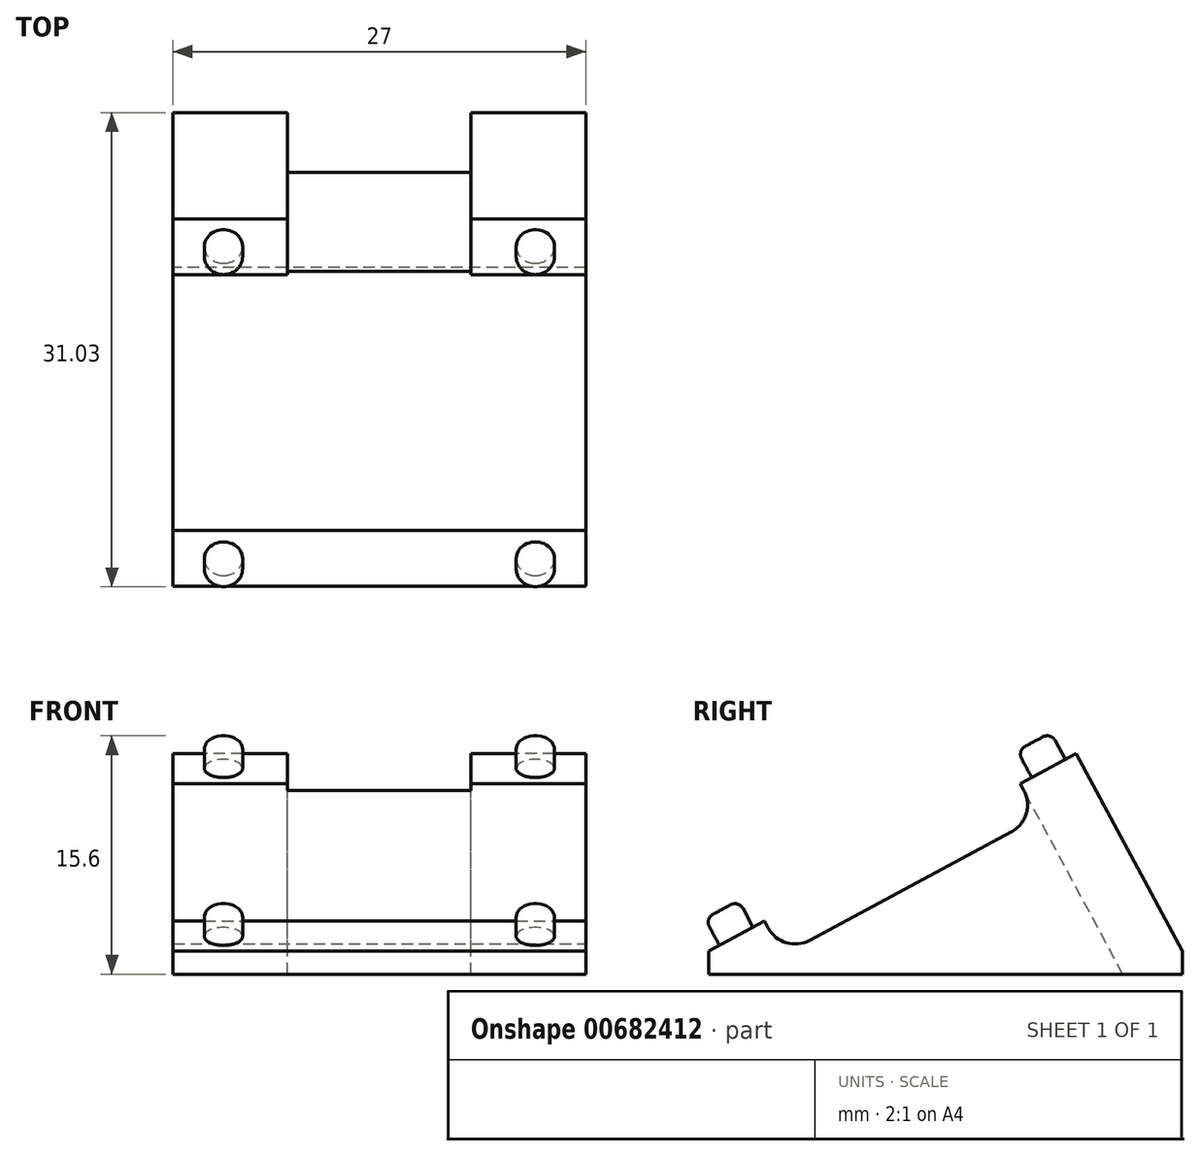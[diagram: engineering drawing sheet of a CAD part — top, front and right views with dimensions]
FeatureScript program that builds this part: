
annotation { "Feature Type Name" : "Feature", "Feature Type Description" : "" }
export const myFeature = defineFeature(function(context is Context, id is Id, definition is map)
    precondition{}
    {
        {
            var Q0;
            Q0=qCreatedBy(makeId("Top.planeOp"),FACE);
            var sketch = newSketch(context, id + "F0", { "sketchPlane" : qUnion([Q0])});
            skLineSegment(sketch, "E0.bottom", {"start": v(-16.53, 19.77) * mm, "end": v(10.47, 19.77) * mm});
            skLineSegment(sketch, "E0.top", {"start": v(-16.53, -11.23) * mm, "end": v(10.47, -11.23) * mm});
            skLineSegment(sketch, "E0.left", {"start": v(-16.53, 19.77) * mm, "end": v(-16.53, -11.23) * mm});
            skLineSegment(sketch, "E0.right", {"start": v(10.47, 19.77) * mm, "end": v(10.47, -11.23) * mm});
            skSolve(sketch);
        }
        {
            var Q0;
            Q0=makeQuery(id+"F0.imprint","IMPRINT",FACE,{"disambiguationData":[TD([[makeQuery(id+"F0.imprint","IMPRINT",EDGE,{"derivedFrom":sQuery(id+"F0.wireOp",EDGE,"E0.bottom")}),-1.0]])]});
            extrude(context, id + "F1", {"entities" : qUnion([Q0]), "depth" : 1.5 * mm, "offsetDistance" : 25 * mm});
        }
        {
            var Q0;
            Q0=makeQuery(id+"F1.opExtrude","SWEPT_FACE",FACE,{"disambiguationData":[OSD([sQuery(id+"F0.wireOp",EDGE,"E0.left")])]});
            var sketch = newSketch(context, id + "F2", { "sketchPlane" : qUnion([Q0])});
            skLineSegment(sketch, "E1", {"start": v(11.23, 1.5) * mm, "end": v(-12.82, 14.43) * mm});
            skLineSegment(sketch, "E2", {"start": v(-12.82, 14.43) * mm, "end": v(-19.77, 1.5) * mm});
            skSolve(sketch);
        }
        {
            var Q0;
            Q0=makeQuery(id+"F2.imprint","IMPRINT",FACE,{"disambiguationData":[TD([[makeQuery(id+"F2.imprint","IMPRINT",EDGE,{"derivedFrom":sQuery(id+"F2.wireOp",EDGE,"E1")}),1.0]])]});
            extrude(context, id + "F3", {"entities" : qUnion([Q0]), "operationType" : NewBodyOperationType.ADD, "oppositeDirection" : true, "depth" : 27 * mm, "offsetDistance" : 25 * mm});
        }
        {
            var Q0;
            Q0=makeQuery(id+"F3.opExtrude","SWEPT_FACE",FACE,{"disambiguationData":[OSD([sQuery(id+"F2.wireOp",EDGE,"E1")])]});
            var sketch = newSketch(context, id + "F4", { "sketchPlane" : qUnion([Q0])});
            skLineSegment(sketch, "E3.bottom", {"start": v(-16.53, 13.98) * mm, "end": v(10.47, 13.98) * mm});
            skLineSegment(sketch, "E3.top", {"start": v(-16.53, -5.02) * mm, "end": v(10.47, -5.02) * mm});
            skLineSegment(sketch, "E3.left", {"start": v(-16.53, 13.98) * mm, "end": v(-16.53, -5.02) * mm});
            skLineSegment(sketch, "E3.right", {"start": v(10.47, 13.98) * mm, "end": v(10.47, -5.02) * mm});
            skPoint(sketch, "E4", {"position": v(-16.53, 4.48) * mm});
            skSolve(sketch);
        }
        {
            var Q0;
            Q0=makeQuery(id+"F4.imprint","IMPRINT",FACE,{"disambiguationData":[TD([[makeQuery(id+"F4.imprint","IMPRINT",EDGE,{"derivedFrom":sQuery(id+"F4.wireOp",EDGE,"E3.bottom")}),-1.0]])]});
            extrude(context, id + "F5", {"entities" : qUnion([Q0]), "operationType" : NewBodyOperationType.REMOVE, "oppositeDirection" : true, "depth" : 2.5 * mm, "offsetDistance" : 25 * mm});
        }
        {
            var Q0;
            Q0=makeQuery(id+"F5.boolean.opBoolean","COPY",EDGE,{"derivedFrom":makeQuery(id+"F5.opExtrude","CAP_EDGE",EDGE,{"disambiguationData":[OSD([sQuery(id+"F4.wireOp",EDGE,"E3.bottom")])],"isStart":false})});
            var Q1;
            Q1=makeQuery(id+"F5.boolean.opBoolean","COPY",EDGE,{"derivedFrom":makeQuery(id+"F5.opExtrude","CAP_EDGE",EDGE,{"disambiguationData":[OSD([sQuery(id+"F4.wireOp",EDGE,"E3.top")])],"isStart":false})});
            fillet(context, id + "F6", {"entities" : qUnion([Q0, Q1]), "radius" : 2 * mm, "tangentPropagation" : true, "allowEdgeOverflow" : false});
        }
        {
            var Q0;
            {var subQ0=sQuery(id+"F2.wireOp",EDGE,"E2");var subQ1=sQuery(id+"F2.wireOp",EDGE,"E1");Q0=makeQuery(id+"F5.boolean.opBoolean","SPLIT",FACE,{"disambiguationData":[TD([makeQuery(id+"F3.opExtrude","SWEPT_FACE",FACE,{"disambiguationData":[OSD([subQ0])]})])],"derivedFrom":makeQuery(id+"F3.opExtrude","SWEPT_FACE",FACE,{"disambiguationData":[OSD([subQ1])]})});}
            var sketch = newSketch(context, id + "F7", { "sketchPlane" : qUnion([Q0])});
            skLineSegment(sketch, "E5.bottom", {"start": v(-9.03, 18.13) * mm, "end": v(2.97, 18.13) * mm});
            skLineSegment(sketch, "E5.top", {"start": v(-9.03, 13.98) * mm, "end": v(2.97, 13.98) * mm});
            skLineSegment(sketch, "E5.left", {"start": v(-9.03, 18.13) * mm, "end": v(-9.03, 13.98) * mm});
            skLineSegment(sketch, "E5.right", {"start": v(2.97, 18.13) * mm, "end": v(2.97, 13.98) * mm});
            skPoint(sketch, "E6", {"position": v(-3.03, 18.13) * mm});
            skSolve(sketch);
        }
        {
            var Q0;
            Q0 = qSketchRegion(id + "F7", true);
            extrude(context, id + "F8", {"entities" : qUnion([Q0]), "operationType" : NewBodyOperationType.REMOVE, "oppositeDirection" : true, "depth" : 25 * mm, "offsetDistance" : 25 * mm});
        }
        {
            var Q0;
            {var subQ1=sQuery(id+"F2.wireOp",EDGE,"E2");var subQ2=makeQuery(id+"F3.opExtrude","SWEPT_FACE",FACE,{"disambiguationData":[OSD([subQ1])]});var subQ3=sQuery(id+"F0.wireOp",EDGE,"E0.left");var subQ4=makeQuery(id+"F1.opExtrude","SWEPT_FACE",FACE,{"disambiguationData":[OSD([subQ3])]});var subQ5=sQuery(id+"F2.wireOp",EDGE,"E1");Q0=makeQuery(id+"F8.boolean.opBoolean","SPLIT",FACE,{"disambiguationData":[TD([subQ4])],"derivedFrom":makeQuery(id+"F5.boolean.opBoolean","SPLIT",FACE,{"disambiguationData":[TD([subQ2])],"derivedFrom":makeQuery(id+"F3.opExtrude","SWEPT_FACE",FACE,{"disambiguationData":[OSD([subQ5])]})})});}
            var sketch = newSketch(context, id + "F9", { "sketchPlane" : qUnion([Q0])});
            skCircle(sketch, "E7", {"center": v(-13.23, 16.08) * mm, "radius": 1.25 * mm});
            skCircle(sketch, "E8", {"center": v(7.17, 16.08) * mm, "radius": 1.25 * mm});
            skCircle(sketch, "E9", {"center": v(-13.23, -7.12) * mm, "radius": 1.25 * mm});
            skCircle(sketch, "E10", {"center": v(7.17, -7.12) * mm, "radius": 1.25 * mm});
            skSolve(sketch);
        }
        {
            var Q0;
            Q0 = qSketchRegion(id + "F9", true);
            extrude(context, id + "F10", {"entities" : qUnion([Q0]), "operationType" : NewBodyOperationType.ADD, "depth" : 2 * mm, "offsetDistance" : 25 * mm});
        }
        {
            var Q0;
            Q0=makeQuery(id+"F10.opExtrude","CAP_EDGE",EDGE,{"disambiguationData":[OSD([sQuery(id+"F9.wireOp",EDGE,"E9")])],"isStart":false});
            var Q1;
            Q1=makeQuery(id+"F10.opExtrude","CAP_EDGE",EDGE,{"disambiguationData":[OSD([sQuery(id+"F9.wireOp",EDGE,"E10")])],"isStart":false});
            var Q2;
            Q2=makeQuery(id+"F10.opExtrude","CAP_EDGE",EDGE,{"disambiguationData":[OSD([sQuery(id+"F9.wireOp",EDGE,"E7")])],"isStart":false});
            var Q3;
            Q3=makeQuery(id+"F10.opExtrude","CAP_EDGE",EDGE,{"disambiguationData":[OSD([sQuery(id+"F9.wireOp",EDGE,"E8")])],"isStart":false});
            fillet(context, id + "F11", {"entities" : qUnion([Q0, Q1, Q2, Q3]), "radius" : 0.6 * mm, "tangentPropagation" : true, "allowEdgeOverflow" : false});
        }
    });
